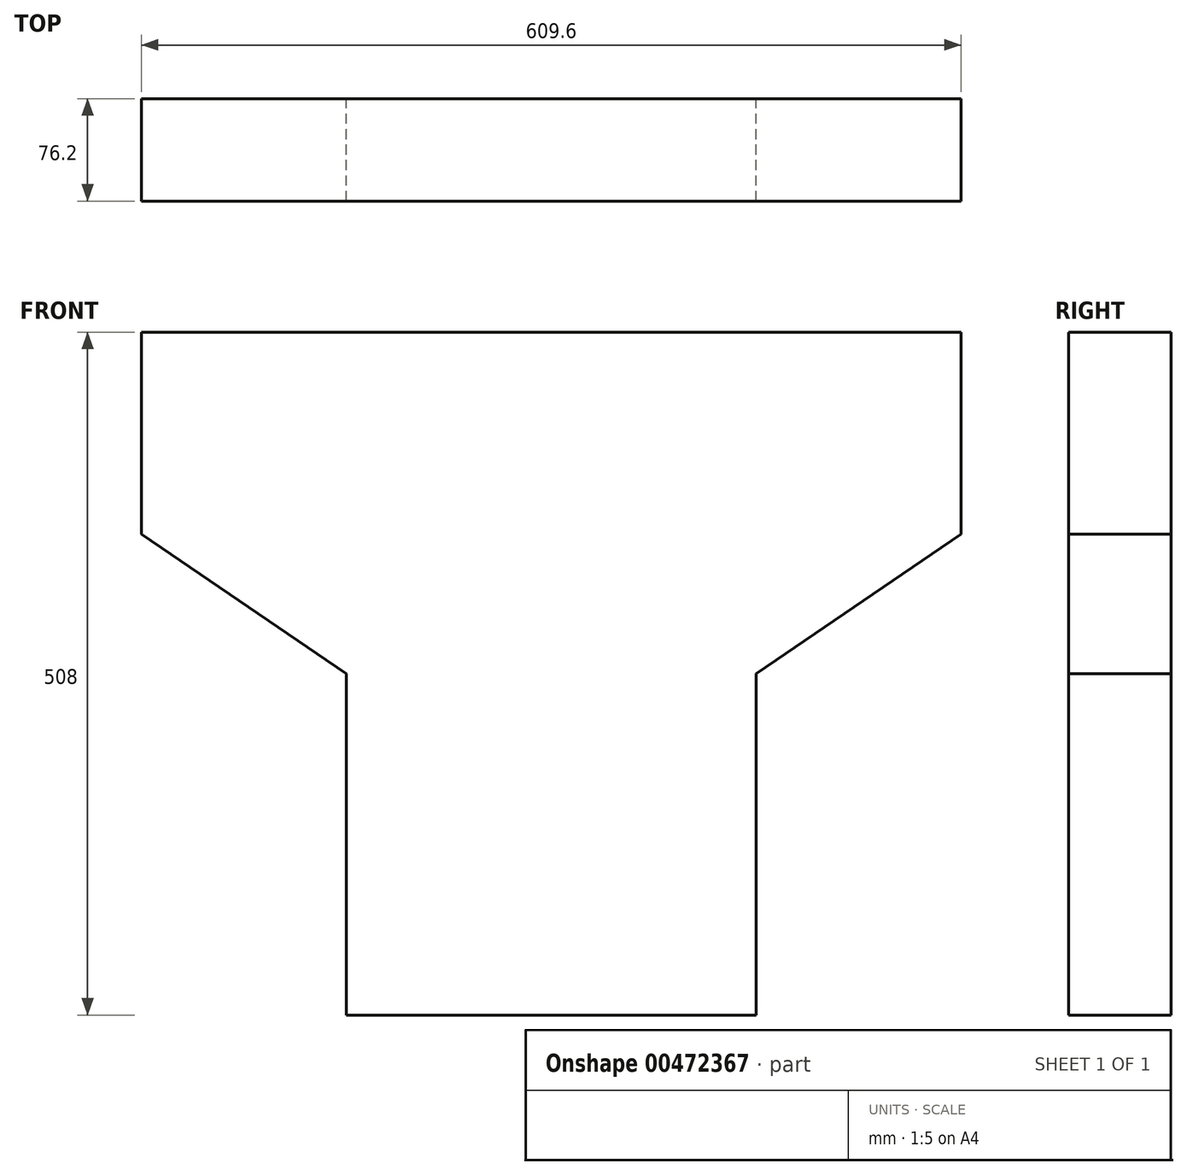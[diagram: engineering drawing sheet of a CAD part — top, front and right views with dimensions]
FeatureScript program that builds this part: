
annotation { "Feature Type Name" : "Feature", "Feature Type Description" : "" }
export const myFeature = defineFeature(function(context is Context, id is Id, definition is map)
    precondition{}
    {
        {
            var Q0;
            Q0=qCreatedBy(makeId("Front.planeOp"),FACE);
            var sketch = newSketch(context, id + "F0", { "sketchPlane" : qUnion([Q0])});
            skLineSegment(sketch, "E0.bottom", {"start": v(-290.75, -261.72) * mm, "end": v(318.85, -261.72) * mm});
            skLineSegment(sketch, "E0.top", {"start": v(-290.75, 246.28) * mm, "end": v(318.85, 246.28) * mm});
            skLineSegment(sketch, "E0.left", {"start": v(-290.75, -261.72) * mm, "end": v(-290.75, 246.28) * mm});
            skLineSegment(sketch, "E0.right", {"start": v(318.85, -261.72) * mm, "end": v(318.85, 246.28) * mm});
            skLineSegment(sketch, "E1", {"start": v(166.45, -261.72) * mm, "end": v(166.45, -7.72) * mm});
            skPoint(sketch, "E1.endSnap0", {"position": v(318.85, -7.72) * mm});
            skLineSegment(sketch, "E2", {"start": v(166.45, -7.72) * mm, "end": v(318.85, 96.04) * mm});
            skLineSegment(sketch, "E3", {"start": v(-138.35, -261.72) * mm, "end": v(-138.35, -7.72) * mm});
            skLineSegment(sketch, "E4", {"start": v(-138.35, -7.72) * mm, "end": v(-290.75, 96.04) * mm});
            skSolve(sketch);
        }
        {
            var Q0;
            {var subQ1=sQuery(id+"F0.wireOp",EDGE,"E0.top");Q0=makeQuery(id+"F0.imprint","IMPRINT",FACE,{"disambiguationData":[TD([[makeQuery(id+"F0.imprint","IMPRINT",EDGE,{"derivedFrom":subQ1}),-1.0]])]});}
            extrude(context, id + "F1", {"entities" : qUnion([Q0]), "depth" : 76.2 * mm});
        }
    });
